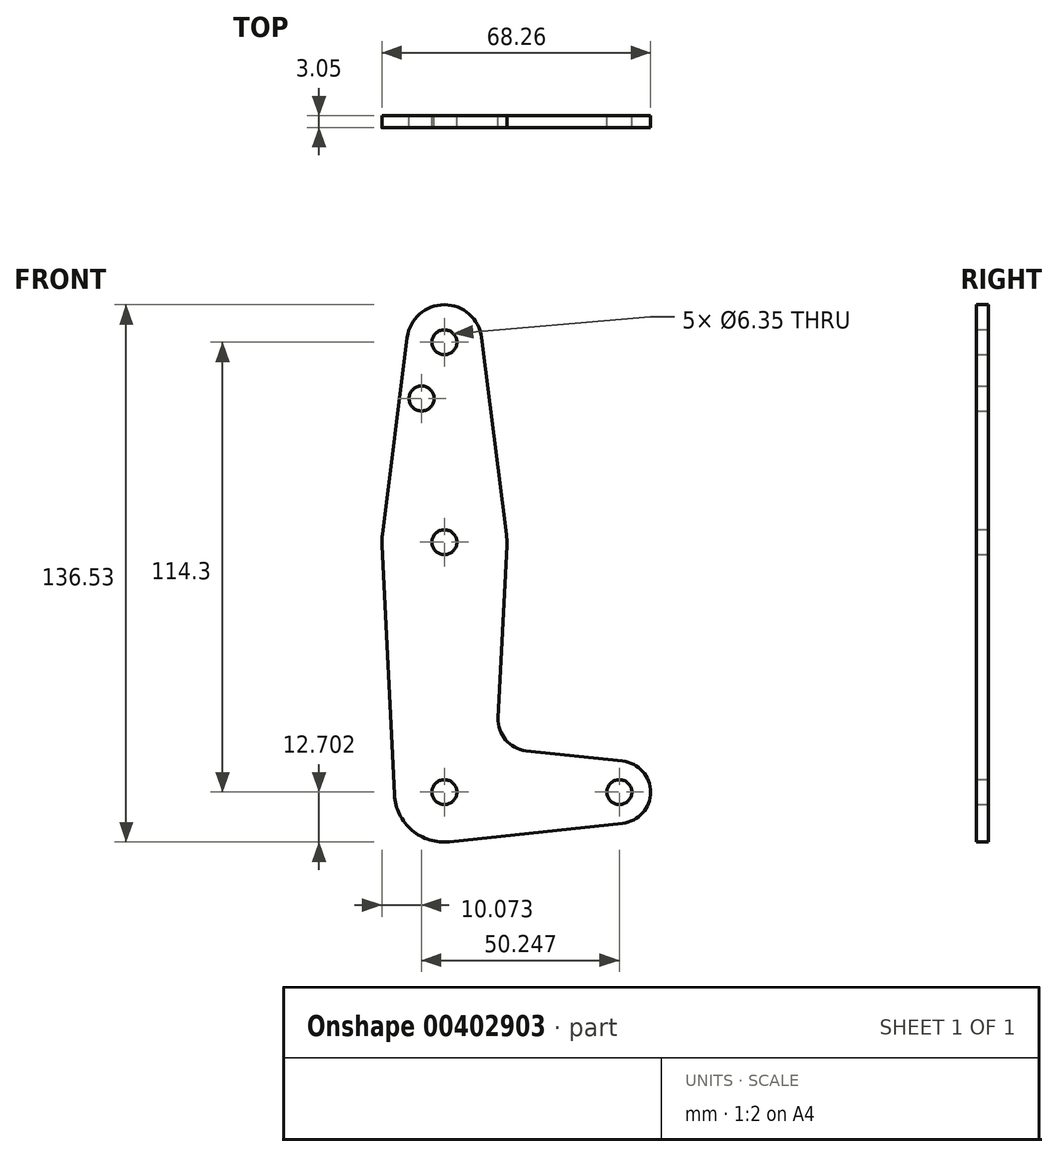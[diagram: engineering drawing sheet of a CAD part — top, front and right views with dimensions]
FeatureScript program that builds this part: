
annotation { "Feature Type Name" : "Feature", "Feature Type Description" : "" }
export const myFeature = defineFeature(function(context is Context, id is Id, definition is map)
    precondition{}
    {
        {
            var Q0;
            Q0=qCreatedBy(makeId("Front.planeOp"),FACE);
            var sketch = newSketch(context, id + "F0", { "sketchPlane" : qUnion([Q0])});
            skLineSegment(sketch, "E0", {"start": v(0, 61.82) * mm, "end": v(0, -52.48) * mm, "construction": true});
            skLineSegment(sketch, "E1", {"start": v(0, -52.48) * mm, "end": v(44.45, -52.48) * mm, "construction": true});
            skCircle(sketch, "E2", {"center": v(0, 61.82) * mm, "radius": 9.53 * mm});
            skCircle(sketch, "E3", {"center": v(0, -52.48) * mm, "radius": 12.7 * mm});
            skCircle(sketch, "E4", {"center": v(44.45, -52.48) * mm, "radius": 7.94 * mm});
            skCircle(sketch, "E5", {"center": v(0, 11.02) * mm, "radius": 15.88 * mm});
            skLineSegment(sketch, "E6", {"start": v(-9.45, 63.01) * mm, "end": v(-15.75, 13) * mm});
            skLineSegment(sketch, "E7", {"start": v(9.45, 63.01) * mm, "end": v(15.75, 13) * mm});
            skLineSegment(sketch, "E8", {"start": v(-15.86, 10.23) * mm, "end": v(-12.68, -53.11) * mm});
            skPoint(sketch, "E9.orphan", {"position": v(0, -39.78) * mm});
            skLineSegment(sketch, "E10", {"start": v(15.86, 10.23) * mm, "end": v(13.66, -33.64) * mm});
            skLineSegment(sketch, "E11", {"start": v(20.75, -41.94) * mm, "end": v(45.3, -44.59) * mm});
            skLineSegment(sketch, "E12", {"start": v(1.36, -65.1) * mm, "end": v(45.3, -60.37) * mm});
            skCircle(sketch, "E13", {"center": v(0, 61.82) * mm, "radius": 3.18 * mm});
            skCircle(sketch, "E14", {"center": v(0, 11.02) * mm, "radius": 3.18 * mm});
            skCircle(sketch, "E15", {"center": v(0, -52.48) * mm, "radius": 3.18 * mm});
            skCircle(sketch, "E16", {"center": v(44.45, -52.48) * mm, "radius": 3.18 * mm});
            skCircle(sketch, "E17", {"center": v(-5.8, 47.55) * mm, "radius": 3.18 * mm});
            skPoint(sketch, "E18.visualSharp", {"position": v(13.28, -41.14) * mm});
            skArc(sketch, "E18.filletArc", {"start": v(13.66, -33.64) * mm, "mid": v(15.55, -39.2) * mm, "end": v(20.75, -41.94) * mm});
            skSolve(sketch);
        }
        {
            var Q0;
            Q0 = qSketchRegion(id + "F0", true);
            extrude(context, id + "F1", {"entities" : qUnion([Q0]), "depth" : 3.05 * mm});
        }
    });
